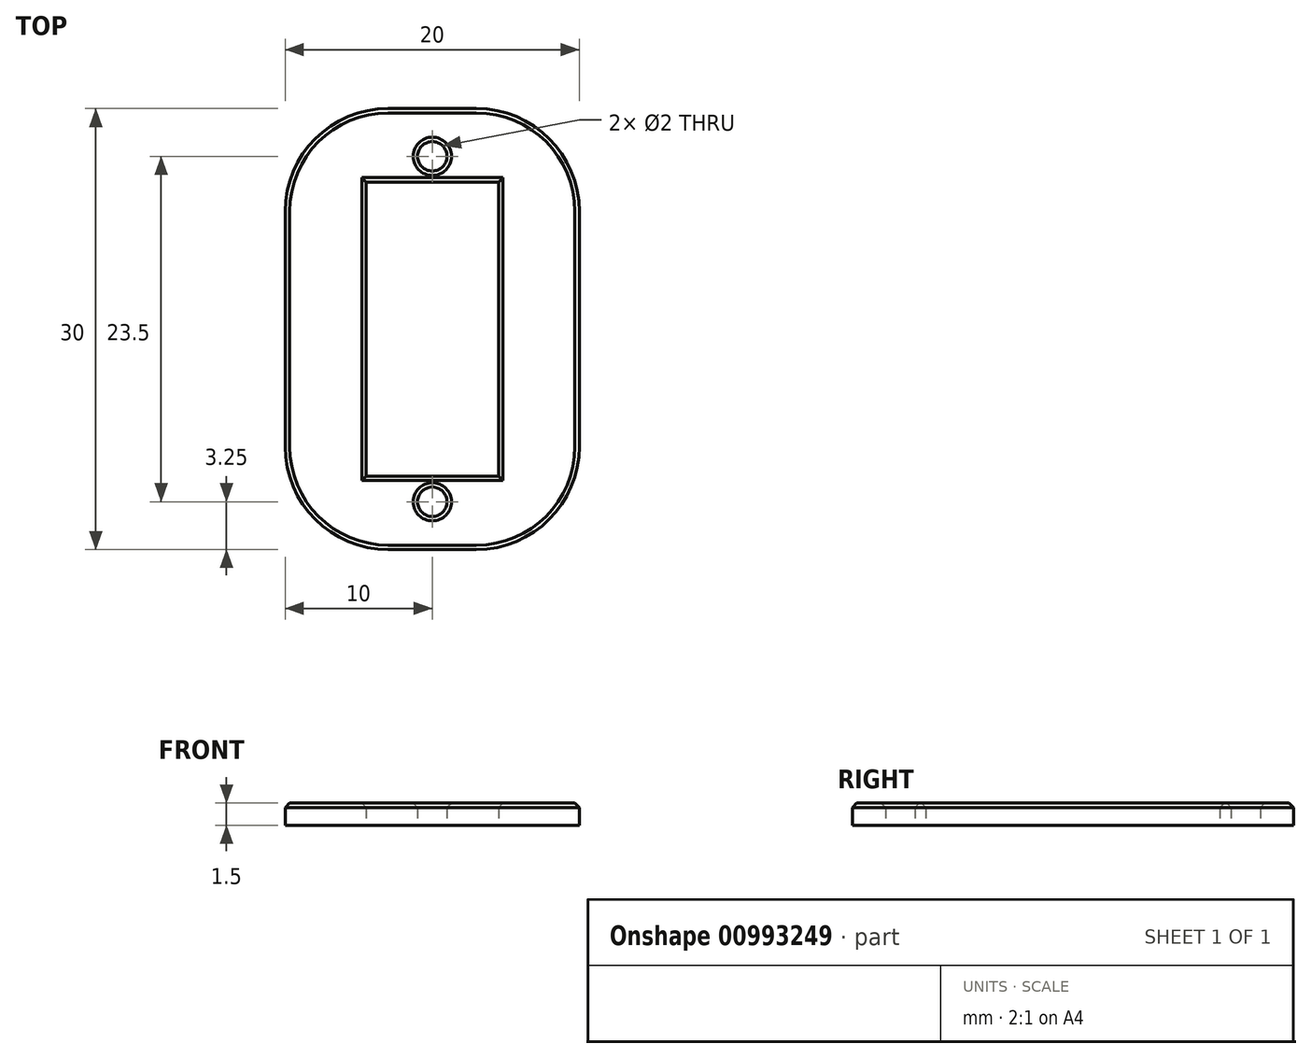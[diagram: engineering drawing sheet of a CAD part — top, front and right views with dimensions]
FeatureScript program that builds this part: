
annotation { "Feature Type Name" : "Feature", "Feature Type Description" : "" }
export const myFeature = defineFeature(function(context is Context, id is Id, definition is map)
    precondition{}
    {
        {
            var Q0;
            Q0=qCreatedBy(makeId("Top.planeOp"),FACE);
            var sketch = newSketch(context, id + "F0", { "sketchPlane" : qUnion([Q0])});
            skLineSegment(sketch, "E0.bottom", {"start": v(4.5, 10) * mm, "end": v(-4.5, 10) * mm});
            skLineSegment(sketch, "E0.top", {"start": v(4.5, -10) * mm, "end": v(-4.5, -10) * mm});
            skLineSegment(sketch, "E0.left", {"start": v(4.5, 10) * mm, "end": v(4.5, -10) * mm});
            skLineSegment(sketch, "E0.right", {"start": v(-4.5, 10) * mm, "end": v(-4.5, -10) * mm});
            skPoint(sketch, "E0.middle", {"position": v(0, 0) * mm});
            skLineSegment(sketch, "E1.bottom", {"start": v(10, -15) * mm, "end": v(-10, -15) * mm});
            skLineSegment(sketch, "E1.top", {"start": v(10, 15) * mm, "end": v(-10, 15) * mm});
            skLineSegment(sketch, "E1.left", {"start": v(10, -15) * mm, "end": v(10, 15) * mm});
            skLineSegment(sketch, "E1.right", {"start": v(-10, -15) * mm, "end": v(-10, 15) * mm});
            skCircle(sketch, "E2", {"center": v(0, -11.75) * mm, "radius": 1 * mm});
            skCircle(sketch, "E3", {"center": v(0, 11.75) * mm, "radius": 1 * mm});
            skLineSegment(sketch, "E4", {"start": v(0, 0) * mm, "end": v(0, 11.75) * mm, "construction": true});
            skLineSegment(sketch, "E5", {"start": v(0, 0) * mm, "end": v(0, -11.75) * mm, "construction": true});
            skSolve(sketch);
        }
        {
            var Q0;
            Q0 = qSketchRegion(id + "F0", true);
            extrude(context, id + "F1", {"entities" : qUnion([Q0]), "depth" : 1.5 * mm, "offsetDistance" : 25 * mm});
        }
        {
            var Q0;
            Q0=makeQuery(id+"F1.opExtrude","SWEPT_EDGE",EDGE,{"disambiguationData":[OSD([sQuery(id+"F0.wireOp",EDGE,"E1.bottom"),sQuery(id+"F0.wireOp",EDGE,"E1.right")])]});
            var Q1;
            Q1=makeQuery(id+"F1.opExtrude","SWEPT_EDGE",EDGE,{"disambiguationData":[OSD([sQuery(id+"F0.wireOp",EDGE,"E1.bottom"),sQuery(id+"F0.wireOp",EDGE,"E1.left")])]});
            var Q2;
            Q2=makeQuery(id+"F1.opExtrude","SWEPT_EDGE",EDGE,{"disambiguationData":[OSD([sQuery(id+"F0.wireOp",EDGE,"E1.top"),sQuery(id+"F0.wireOp",EDGE,"E1.left")])]});
            var Q3;
            Q3=makeQuery(id+"F1.opExtrude","SWEPT_EDGE",EDGE,{"disambiguationData":[OSD([sQuery(id+"F0.wireOp",EDGE,"E1.top"),sQuery(id+"F0.wireOp",EDGE,"E1.right")])]});
            fillet(context, id + "F2", {"entities" : qUnion([Q0, Q1, Q2, Q3]), "radius" : 7 * mm, "tangentPropagation" : true, "allowEdgeOverflow" : false});
        }
        {
            var Q0;
            Q0=makeQuery(id+"F1.opExtrude","CAP_EDGE",EDGE,{"disambiguationData":[OSD([sQuery(id+"F0.wireOp",EDGE,"E2")])],"isStart":false});
            var Q1;
            Q1=makeQuery(id+"F1.opExtrude","CAP_EDGE",EDGE,{"disambiguationData":[OSD([sQuery(id+"F0.wireOp",EDGE,"E3")])],"isStart":false});
            var Q2;
            Q2=makeQuery(id+"F1.opExtrude","CAP_EDGE",EDGE,{"disambiguationData":[OSD([sQuery(id+"F0.wireOp",EDGE,"E0.bottom")])],"isStart":false});
            var Q3;
            Q3=makeQuery(id+"F1.opExtrude","CAP_EDGE",EDGE,{"disambiguationData":[OSD([sQuery(id+"F0.wireOp",EDGE,"E0.right")])],"isStart":false});
            var Q4;
            Q4=makeQuery(id+"F1.opExtrude","CAP_EDGE",EDGE,{"disambiguationData":[OSD([sQuery(id+"F0.wireOp",EDGE,"E0.top")])],"isStart":false});
            var Q5;
            Q5=makeQuery(id+"F1.opExtrude","CAP_EDGE",EDGE,{"disambiguationData":[OSD([sQuery(id+"F0.wireOp",EDGE,"E0.left")])],"isStart":false});
            var Q6;
            Q6=makeQuery(id+"F1.opExtrude","CAP_EDGE",EDGE,{"disambiguationData":[OSD([sQuery(id+"F0.wireOp",EDGE,"E1.top")])],"isStart":false});
            var Q7;
            {var subQ0=sQuery(id+"F0.wireOp",EDGE,"E1.right");var subQ1=sQuery(id+"F0.wireOp",EDGE,"E1.top");Q7=makeQuery(id+"F2.opFillet","BLEND_EDGE",EDGE,{"blendedFrom":[makeQuery(id+"F1.opExtrude","SWEPT_EDGE",EDGE,{"disambiguationData":[OSD([subQ1,subQ0])]}),makeQuery(id+"F1.opExtrude","CAP_FACE",FACE,{"disambiguationData":[OSD([sQuery(id+"F0.wireOp",EDGE,"E0.bottom"),sQuery(id+"F0.wireOp",EDGE,"E0.top"),sQuery(id+"F0.wireOp",EDGE,"E0.left"),sQuery(id+"F0.wireOp",EDGE,"E0.right"),sQuery(id+"F0.wireOp",EDGE,"E1.bottom"),subQ1,sQuery(id+"F0.wireOp",EDGE,"E1.left"),subQ0,sQuery(id+"F0.wireOp",EDGE,"E2"),sQuery(id+"F0.wireOp",EDGE,"E3")])],"isStart":false})],"blendedInto":[makeQuery(id+"F1.opExtrude","CAP_FACE",FACE,{"disambiguationData":[OSD([sQuery(id+"F0.wireOp",EDGE,"E0.bottom"),sQuery(id+"F0.wireOp",EDGE,"E0.top"),sQuery(id+"F0.wireOp",EDGE,"E0.left"),sQuery(id+"F0.wireOp",EDGE,"E0.right"),sQuery(id+"F0.wireOp",EDGE,"E1.bottom"),subQ1,sQuery(id+"F0.wireOp",EDGE,"E1.left"),subQ0,sQuery(id+"F0.wireOp",EDGE,"E2"),sQuery(id+"F0.wireOp",EDGE,"E3")])],"isStart":false})]});}
            var Q8;
            Q8=makeQuery(id+"F1.opExtrude","CAP_EDGE",EDGE,{"disambiguationData":[OSD([sQuery(id+"F0.wireOp",EDGE,"E1.right")])],"isStart":false});
            var Q9;
            {var subQ0=sQuery(id+"F0.wireOp",EDGE,"E1.left");var subQ1=sQuery(id+"F0.wireOp",EDGE,"E1.top");Q9=makeQuery(id+"F2.opFillet","BLEND_EDGE",EDGE,{"blendedFrom":[makeQuery(id+"F1.opExtrude","SWEPT_EDGE",EDGE,{"disambiguationData":[OSD([subQ1,subQ0])]}),makeQuery(id+"F1.opExtrude","CAP_FACE",FACE,{"disambiguationData":[OSD([sQuery(id+"F0.wireOp",EDGE,"E0.bottom"),sQuery(id+"F0.wireOp",EDGE,"E0.top"),sQuery(id+"F0.wireOp",EDGE,"E0.left"),sQuery(id+"F0.wireOp",EDGE,"E0.right"),sQuery(id+"F0.wireOp",EDGE,"E1.bottom"),subQ1,subQ0,sQuery(id+"F0.wireOp",EDGE,"E1.right"),sQuery(id+"F0.wireOp",EDGE,"E2"),sQuery(id+"F0.wireOp",EDGE,"E3")])],"isStart":false})],"blendedInto":[makeQuery(id+"F1.opExtrude","CAP_FACE",FACE,{"disambiguationData":[OSD([sQuery(id+"F0.wireOp",EDGE,"E0.bottom"),sQuery(id+"F0.wireOp",EDGE,"E0.top"),sQuery(id+"F0.wireOp",EDGE,"E0.left"),sQuery(id+"F0.wireOp",EDGE,"E0.right"),sQuery(id+"F0.wireOp",EDGE,"E1.bottom"),subQ1,subQ0,sQuery(id+"F0.wireOp",EDGE,"E1.right"),sQuery(id+"F0.wireOp",EDGE,"E2"),sQuery(id+"F0.wireOp",EDGE,"E3")])],"isStart":false})]});}
            var Q10;
            Q10=makeQuery(id+"F1.opExtrude","CAP_EDGE",EDGE,{"disambiguationData":[OSD([sQuery(id+"F0.wireOp",EDGE,"E1.left")])],"isStart":false});
            var Q11;
            {var subQ0=sQuery(id+"F0.wireOp",EDGE,"E1.left");var subQ1=sQuery(id+"F0.wireOp",EDGE,"E1.bottom");Q11=makeQuery(id+"F2.opFillet","BLEND_EDGE",EDGE,{"blendedFrom":[makeQuery(id+"F1.opExtrude","SWEPT_EDGE",EDGE,{"disambiguationData":[OSD([subQ1,subQ0])]}),makeQuery(id+"F1.opExtrude","CAP_FACE",FACE,{"disambiguationData":[OSD([sQuery(id+"F0.wireOp",EDGE,"E0.bottom"),sQuery(id+"F0.wireOp",EDGE,"E0.top"),sQuery(id+"F0.wireOp",EDGE,"E0.left"),sQuery(id+"F0.wireOp",EDGE,"E0.right"),subQ1,sQuery(id+"F0.wireOp",EDGE,"E1.top"),subQ0,sQuery(id+"F0.wireOp",EDGE,"E1.right"),sQuery(id+"F0.wireOp",EDGE,"E2"),sQuery(id+"F0.wireOp",EDGE,"E3")])],"isStart":false})],"blendedInto":[makeQuery(id+"F1.opExtrude","CAP_FACE",FACE,{"disambiguationData":[OSD([sQuery(id+"F0.wireOp",EDGE,"E0.bottom"),sQuery(id+"F0.wireOp",EDGE,"E0.top"),sQuery(id+"F0.wireOp",EDGE,"E0.left"),sQuery(id+"F0.wireOp",EDGE,"E0.right"),subQ1,sQuery(id+"F0.wireOp",EDGE,"E1.top"),subQ0,sQuery(id+"F0.wireOp",EDGE,"E1.right"),sQuery(id+"F0.wireOp",EDGE,"E2"),sQuery(id+"F0.wireOp",EDGE,"E3")])],"isStart":false})]});}
            var Q12;
            Q12=makeQuery(id+"F1.opExtrude","CAP_EDGE",EDGE,{"disambiguationData":[OSD([sQuery(id+"F0.wireOp",EDGE,"E1.bottom")])],"isStart":false});
            var Q13;
            {var subQ0=sQuery(id+"F0.wireOp",EDGE,"E1.right");var subQ1=sQuery(id+"F0.wireOp",EDGE,"E1.bottom");Q13=makeQuery(id+"F2.opFillet","BLEND_EDGE",EDGE,{"blendedFrom":[makeQuery(id+"F1.opExtrude","SWEPT_EDGE",EDGE,{"disambiguationData":[OSD([subQ1,subQ0])]}),makeQuery(id+"F1.opExtrude","CAP_FACE",FACE,{"disambiguationData":[OSD([sQuery(id+"F0.wireOp",EDGE,"E0.bottom"),sQuery(id+"F0.wireOp",EDGE,"E0.top"),sQuery(id+"F0.wireOp",EDGE,"E0.left"),sQuery(id+"F0.wireOp",EDGE,"E0.right"),subQ1,sQuery(id+"F0.wireOp",EDGE,"E1.top"),sQuery(id+"F0.wireOp",EDGE,"E1.left"),subQ0,sQuery(id+"F0.wireOp",EDGE,"E2"),sQuery(id+"F0.wireOp",EDGE,"E3")])],"isStart":false})],"blendedInto":[makeQuery(id+"F1.opExtrude","CAP_FACE",FACE,{"disambiguationData":[OSD([sQuery(id+"F0.wireOp",EDGE,"E0.bottom"),sQuery(id+"F0.wireOp",EDGE,"E0.top"),sQuery(id+"F0.wireOp",EDGE,"E0.left"),sQuery(id+"F0.wireOp",EDGE,"E0.right"),subQ1,sQuery(id+"F0.wireOp",EDGE,"E1.top"),sQuery(id+"F0.wireOp",EDGE,"E1.left"),subQ0,sQuery(id+"F0.wireOp",EDGE,"E2"),sQuery(id+"F0.wireOp",EDGE,"E3")])],"isStart":false})]});}
            chamfer(context, id + "F3", {"entities" : qUnion([Q0, Q1, Q2, Q3, Q4, Q5, Q6, Q7, Q8, Q9, Q10, Q11, Q12, Q13]), "width" : 0.3 * mm, "tangentPropagation" : true});
        }
    });
